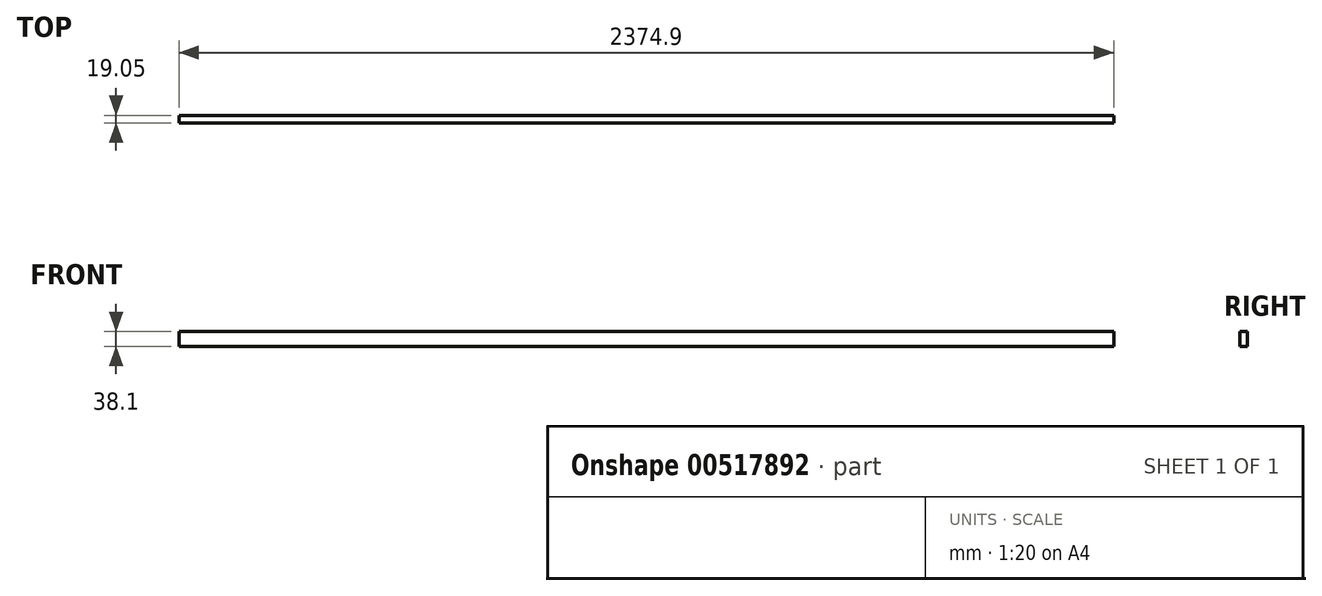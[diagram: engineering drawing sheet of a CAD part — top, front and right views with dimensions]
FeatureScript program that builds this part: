
annotation { "Feature Type Name" : "Feature", "Feature Type Description" : "" }
export const myFeature = defineFeature(function(context is Context, id is Id, definition is map)
    precondition{}
    {
        {
            var Q0;
            Q0=qCreatedBy(makeId("Right.planeOp"),FACE);
            var sketch = newSketch(context, id + "F0", { "sketchPlane" : qUnion([Q0])});
            skLineSegment(sketch, "E0.bottom", {"start": v(0, 0) * mm, "end": v(19.05, 0) * mm});
            skLineSegment(sketch, "E0.top", {"start": v(0, 38.1) * mm, "end": v(19.05, 38.1) * mm});
            skLineSegment(sketch, "E0.left", {"start": v(0, 0) * mm, "end": v(0, 38.1) * mm});
            skLineSegment(sketch, "E0.right", {"start": v(19.05, 0) * mm, "end": v(19.05, 38.1) * mm});
            skLineSegment(sketch, "E1.0", {"start": v(3.17, 34.93) * mm, "end": v(15.87, 34.93) * mm, "construction": true});
            skLineSegment(sketch, "E1.1", {"start": v(3.17, 3.17) * mm, "end": v(3.17, 34.93) * mm, "construction": true});
            skLineSegment(sketch, "E1.2", {"start": v(3.17, 3.17) * mm, "end": v(15.88, 3.17) * mm, "construction": true});
            skLineSegment(sketch, "E1.3", {"start": v(15.88, 3.17) * mm, "end": v(15.87, 34.93) * mm, "construction": true});
            skSolve(sketch);
        }
        {
            var Q0;
            Q0 = qSketchRegion(id + "F0", true);
            extrude(context, id + "F1", {"entities" : qUnion([Q0]), "oppositeDirection" : true, "depth" : 2374.9 * mm, "offsetDistance" : 25.4 * mm});
        }
    });
